# Revit family: Скамейка уличная «Палермо натур»
name_source: partatom
category: Мебель
revit_build: Autodesk Revit 2017 (Build: 20160225_1515(x64)
units: mm (PartAtom-declared; Revit-internal decimal feet)

## family parameters
Всегда вертикально = Да
Заголовок OmniClass = General Furniture and Specialties
На основе рабочей плоскости = Нет
Номер OmniClass = 23.40.20.00
Общий = Нет
При загрузке вырезать с полостями = Нет
Точка расчета площади = Нет

## types (2) — shared parameters
ADSK_Код изделия = 9675
ADSK_Материал доски = <По категории>
ADSK_Материал опоры = <По категории>
ADSK_Размер_Высота = 980 мм
ADSK_Размер_Высота сидения = 452 мм
ADSK_Размер_Ширина = 733 мм
ADSK_Размер_Ширина сидения = 535 мм
URL = https://hobbyka.ru
Изготовитель = ООО "Хоббика"

## per-type parameters (varying)
| type | ADSK_Размер_Длина | Стоимость |
| Скамейка уличная «Палермо» 1.8м | 1512 мм | 40110 $ |
| Скамейка уличная «Палермо натур» 3,0м | 3000 мм | 56175 $ |

note: column(s) folded — value = type name in every type: ADSK_Наименование
